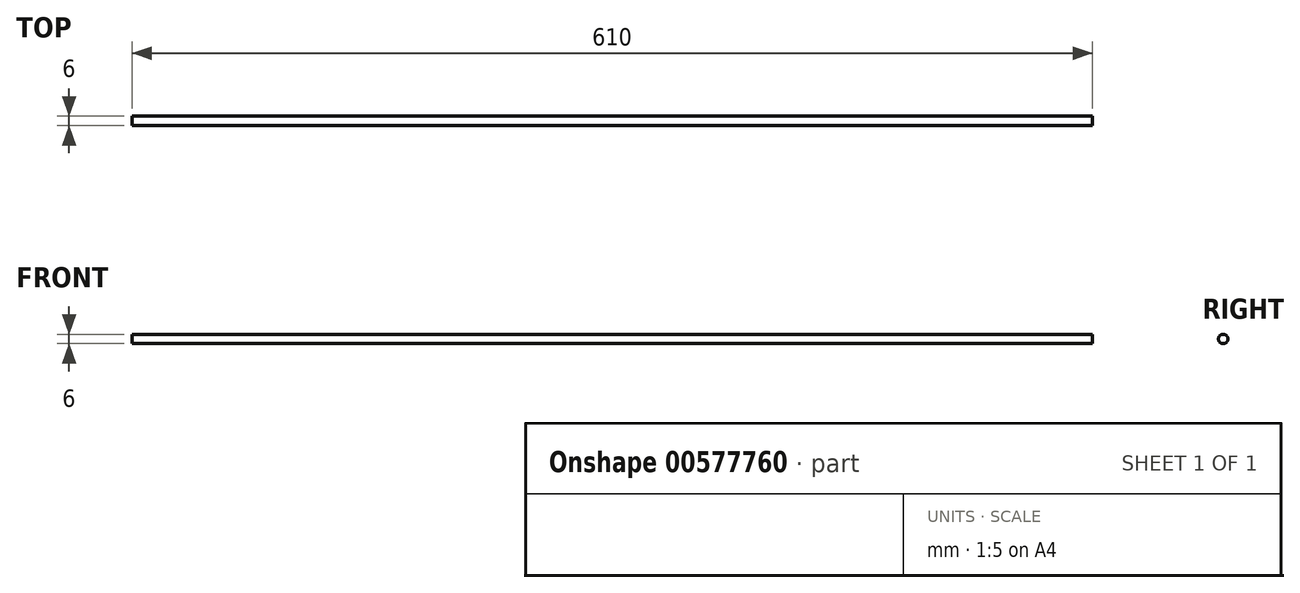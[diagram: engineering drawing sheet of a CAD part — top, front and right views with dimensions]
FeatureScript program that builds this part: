
annotation { "Feature Type Name" : "Feature", "Feature Type Description" : "" }
export const myFeature = defineFeature(function(context is Context, id is Id, definition is map)
    precondition{}
    {
        {
            var Q0;
            Q0=qCreatedBy(makeId("Right.planeOp"),FACE);
            var sketch = newSketch(context, id + "F0", { "sketchPlane" : qUnion([Q0])});
            skCircle(sketch, "E0", {"center": v(0, 0) * mm, "radius": 3 * mm});
            skSolve(sketch);
        }
        {
            var Q0;
            Q0 = qSketchRegion(id + "F0", true);
            extrude(context, id + "F1", {"entities" : qUnion([Q0]), "endBound" : BoundingType.SYMMETRIC, "depth" : 610 * mm, "offsetDistance" : 25 * mm});
        }
    });
